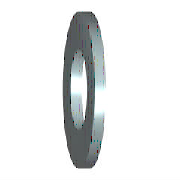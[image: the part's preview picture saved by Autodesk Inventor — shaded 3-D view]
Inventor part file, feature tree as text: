
AUTODESK INVENTOR PART (.ipt)
format: ipt  version: 2023.1 (Build 271208000, 208)  size: 122,880 bytes
history: native  units: mm (DEFAULTED — no unit token found)
features: other x1, plane x1, sketch x1
ambient origin geometry x7: Origin, YZ Plane, XY Plane, X Axis, Y Axis, Z Axis, Center Point
bodies: Solid1 (feature_tree), Body (feature_tree)
feature tree (3):
  other  "Work Axis1"
  plane  "Work Plane1"
  sketch  "Sketch"  dims[d0=3.5814mm d1=7.1374mm d2=0.8128mm d3=0.0mm d4=0.0mm d5=0.0mm d6=0.0mm d7=0.0mm]
